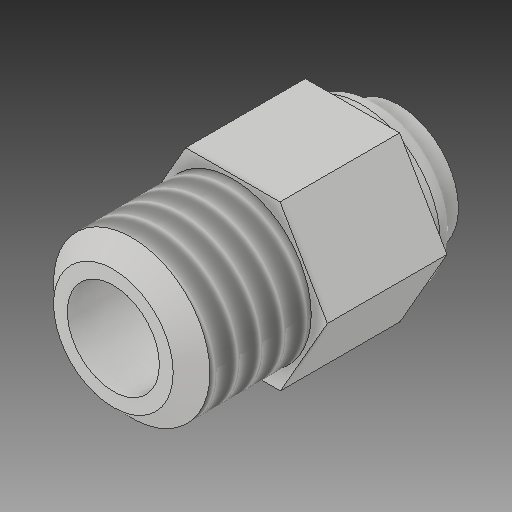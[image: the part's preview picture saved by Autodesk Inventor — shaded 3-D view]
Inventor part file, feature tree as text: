
AUTODESK INVENTOR PART (.ipt)
format: ipt  version: 2018 (Build 220112000, 112)  size: 177,152 bytes
history: native  units: mm
features: sketch x6, other x3
ambient origin geometry x8: Origin, YZ Plane, XZ Plane, XY Plane, X Axis, Y Axis, Z Axis, Center Point
bodies: Solid1 (feature_tree)
feature tree (9):
  other  "Pushfit-Adapter.ipt"
  other  "Solid1::Pushfit-Adapter.ipt"
  other  "TaggingFeature1"
  sketch  "Sketch1"  dims[d0=10.0mm]
  sketch  "Sketch2"
  sketch  "Sketch3"
  sketch  "Sketch4"
  sketch  "Sketch5"
  sketch  "Sketch6"
